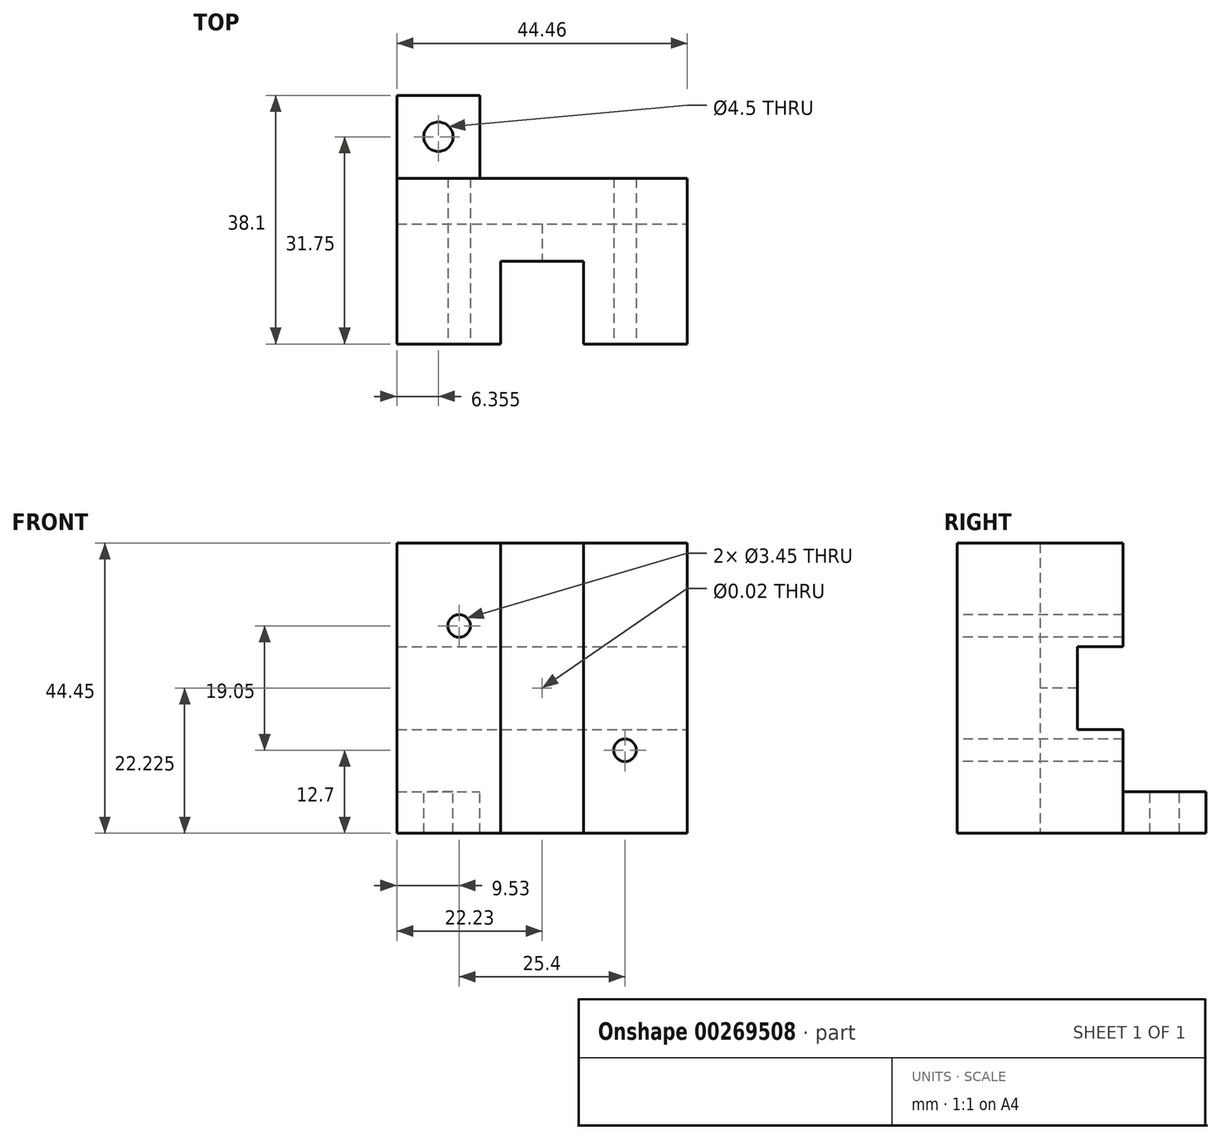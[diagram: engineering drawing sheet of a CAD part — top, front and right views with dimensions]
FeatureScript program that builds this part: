
annotation { "Feature Type Name" : "Feature", "Feature Type Description" : "" }
export const myFeature = defineFeature(function(context is Context, id is Id, definition is map)
    precondition{}
    {
        {
            var Q0;
            Q0=qCreatedBy(makeId("Top.planeOp"),FACE);
            var sketch = newSketch(context, id + "F0", { "sketchPlane" : qUnion([Q0])});
            skLineSegment(sketch, "E0.bottom", {"start": v(22.23, -12.7) * mm, "end": v(-22.23, -12.7) * mm});
            skLineSegment(sketch, "E0.top", {"start": v(22.23, 12.7) * mm, "end": v(-22.23, 12.7) * mm});
            skLineSegment(sketch, "E0.left", {"start": v(22.23, -12.7) * mm, "end": v(22.23, 12.7) * mm});
            skLineSegment(sketch, "E0.right", {"start": v(-22.23, -12.7) * mm, "end": v(-22.23, 12.7) * mm});
            skPoint(sketch, "E0.middle", {"position": v(0, 0) * mm});
            skSolve(sketch);
        }
        {
            var Q0;
            Q0=qSketchRegion(id+"F0",true);
            extrude(context, id + "F1", {"entities" : qUnion([Q0]), "depth" : 44.45 * mm});
        }
        {
            var Q0;
            Q0=makeQuery(id+"F1.opExtrude","SWEPT_FACE",FACE,{"disambiguationData":[OSD([sQuery(id+"F0.wireOp",EDGE,"E0.bottom")])]});
            var sketch = newSketch(context, id + "F2", { "sketchPlane" : qUnion([Q0])});
            skLineSegment(sketch, "E1.bottom", {"start": v(6.35, 44.45) * mm, "end": v(-6.35, 44.45) * mm});
            skLineSegment(sketch, "E1.top", {"start": v(6.35, 0) * mm, "end": v(-6.35, 0) * mm});
            skLineSegment(sketch, "E1.left", {"start": v(6.35, 44.45) * mm, "end": v(6.35, 0) * mm});
            skLineSegment(sketch, "E1.right", {"start": v(-6.35, 44.45) * mm, "end": v(-6.35, 0) * mm});
            skPoint(sketch, "E1.middle", {"position": v(0, 22.23) * mm});
            skSolve(sketch);
        }
        {
            var Q0;
            Q0=qSketchRegion(id+"F2",true);
            extrude(context, id + "F3", {"entities" : qUnion([Q0]), "operationType" : NewBodyOperationType.REMOVE, "oppositeDirection" : true, "depth" : 12.7 * mm});
        }
        {
            var Q0;
            Q0=makeQuery(id+"F1.opExtrude","SWEPT_FACE",FACE,{"disambiguationData":[OSD([sQuery(id+"F0.wireOp",EDGE,"E0.top")])]});
            var sketch = newSketch(context, id + "F4", { "sketchPlane" : qUnion([Q0])});
            skLineSegment(sketch, "E2.bottom", {"start": v(22.23, 15.88) * mm, "end": v(-22.23, 15.88) * mm});
            skLineSegment(sketch, "E2.top", {"start": v(22.23, 28.58) * mm, "end": v(-22.23, 28.58) * mm});
            skLineSegment(sketch, "E2.left", {"start": v(22.23, 15.88) * mm, "end": v(22.23, 28.58) * mm});
            skLineSegment(sketch, "E2.right", {"start": v(-22.23, 15.88) * mm, "end": v(-22.23, 28.58) * mm});
            skPoint(sketch, "E2.middle", {"position": v(0, 22.23) * mm});
            skPoint(sketch, "E2.middle.positionSnap0", {"position": v(22.23, 22.23) * mm});
            skPoint(sketch, "E2.middle.positionSnap1", {"position": v(0, 0) * mm});
            skPoint(sketch, "E2.centerSnap0", {"position": v(22.23, 22.23) * mm});
            skPoint(sketch, "E2.centerSnap1", {"position": v(0, 0) * mm});
            skSolve(sketch);
        }
        {
            var Q0;
            Q0=qSketchRegion(id+"F4",true);
            extrude(context, id + "F5", {"entities" : qUnion([Q0]), "operationType" : NewBodyOperationType.REMOVE, "oppositeDirection" : true, "depth" : 7 * mm});
        }
        {
            var Q0;
            {var subQ0=sQuery(id+"F0.wireOp",EDGE,"E0.right");var subQ3=sQuery(id+"F0.wireOp",EDGE,"E0.bottom");Q0=makeQuery(id+"F3.boolean.opBoolean","SPLIT",FACE,{"disambiguationData":[TD([makeQuery(id+"F1.opExtrude","SWEPT_FACE",FACE,{"disambiguationData":[OSD([subQ0])]})])],"derivedFrom":makeQuery(id+"F1.opExtrude","SWEPT_FACE",FACE,{"disambiguationData":[OSD([subQ3])]})});}
            var sketch = newSketch(context, id + "F6", { "sketchPlane" : qUnion([Q0])});
            skPoint(sketch, "E3", {"position": v(0, 22.23) * mm});
            skPoint(sketch, "E3.positionSnap0", {"position": v(-22.23, 22.23) * mm});
            skSolve(sketch);
        }
        {
            var Q0;
            Q0=sQuery(id+"F6.wireOp",VERTEX,"E3");
            var Q1;
            Q1=makeQuery(id+"F1.opExtrude","SWEPT_BODY",BODY,{"disambiguationData":[OSD([sQuery(id+"F0.wireOp",EDGE,"E0.bottom"),sQuery(id+"F0.wireOp",EDGE,"E0.top"),sQuery(id+"F0.wireOp",EDGE,"E0.left"),sQuery(id+"F0.wireOp",EDGE,"E0.right")])]});
            hole(context, id + "F7", {"style" : HoleStyle.SIMPLE, "endStyle" : HoleEndStyle.THROUGH, "standardTappedOrClearance" : lookupTablePath({ "standard" : "ANSI", "size" : "1/2 (0.5)", "type" : "Drilled" }), "standardBlindInLast" : lookupTablePath({ "standard" : "ANSI", "size" : "1/2", "type" : "Drilled" }), "holeDiameter" : 1 / 50.8 * mm, "tappedDepth" : 10.16 * mm, "tapClearance" : 3, "locations" : qUnion([Q0]), "scope" : qUnion([Q1])});
        }
        {
            var Q0;
            {var subQ2=sQuery(id+"F0.wireOp",EDGE,"E0.top");Q0=makeQuery(id+"F5.boolean.opBoolean","SPLIT",FACE,{"disambiguationData":[TD([makeQuery(id+"F5.opExtrude","SWEPT_FACE",FACE,{"disambiguationData":[OSD([sQuery(id+"F4.wireOp",EDGE,"E2.bottom")])]})])],"derivedFrom":makeQuery(id+"F1.opExtrude","SWEPT_FACE",FACE,{"disambiguationData":[OSD([subQ2])]})});}
            var sketch = newSketch(context, id + "F8", { "sketchPlane" : qUnion([Q0])});
            skLineSegment(sketch, "E4.bottom", {"start": v(22.23, 0) * mm, "end": v(9.52, 0) * mm});
            skLineSegment(sketch, "E4.top", {"start": v(22.23, 6.35) * mm, "end": v(9.52, 6.35) * mm});
            skLineSegment(sketch, "E4.left", {"start": v(22.23, 0) * mm, "end": v(22.23, 6.35) * mm});
            skLineSegment(sketch, "E4.right", {"start": v(9.53, 0) * mm, "end": v(9.52, 6.35) * mm});
            skSolve(sketch);
        }
        {
            var Q0;
            Q0=qSketchRegion(id+"F8",true);
            extrude(context, id + "F9", {"entities" : qUnion([Q0]), "operationType" : NewBodyOperationType.ADD, "depth" : 12.7 * mm});
        }
        {
            var Q0;
            Q0=makeQuery(id+"F9.opExtrude","SWEPT_FACE",FACE,{"disambiguationData":[OSD([sQuery(id+"F8.wireOp",EDGE,"E4.top")])]});
            var sketch = newSketch(context, id + "F10", { "sketchPlane" : qUnion([Q0])});
            skPoint(sketch, "E5", {"position": v(-15.88, 19.05) * mm});
            skPoint(sketch, "E5.positionSnap0", {"position": v(-15.88, 25.4) * mm});
            skPoint(sketch, "E5.positionSnap1", {"position": v(-9.53, 19.05) * mm});
            skSolve(sketch);
        }
        {
            var Q0;
            Q0=sQuery(id+"F10.wireOp",VERTEX,"E5");
            var Q1;
            Q1=makeQuery(id+"F1.opExtrude","SWEPT_BODY",BODY,{"disambiguationData":[OSD([sQuery(id+"F0.wireOp",EDGE,"E0.bottom"),sQuery(id+"F0.wireOp",EDGE,"E0.top"),sQuery(id+"F0.wireOp",EDGE,"E0.left"),sQuery(id+"F0.wireOp",EDGE,"E0.right")])]});
            hole(context, id + "F11", {"style" : HoleStyle.SIMPLE, "endStyle" : HoleEndStyle.THROUGH, "standardTappedOrClearance" : lookupTablePath({ "standard" : "ANSI", "fit" : "Normal (ASME)", "size" : "#8", "type" : "Clearance" }), "standardBlindInLast" : lookupTablePath({ "fit" : "Free", "standard" : "ANSI", "size" : "#8", "type" : "Clearance" }), "holeDiameter" : 4.5 * mm, "tappedDepth" : 9.52 * mm, "tapClearance" : 3, "locations" : qUnion([Q0]), "scope" : qUnion([Q1])});
        }
        {
            var Q0;
            {var subQ0=sQuery(id+"F0.wireOp",EDGE,"E0.right");var subQ3=sQuery(id+"F0.wireOp",EDGE,"E0.bottom");Q0=makeQuery(id+"F3.boolean.opBoolean","SPLIT",FACE,{"disambiguationData":[TD([makeQuery(id+"F1.opExtrude","SWEPT_FACE",FACE,{"disambiguationData":[OSD([subQ0])]})])],"derivedFrom":makeQuery(id+"F1.opExtrude","SWEPT_FACE",FACE,{"disambiguationData":[OSD([subQ3])]})});}
            var sketch = newSketch(context, id + "F12", { "sketchPlane" : qUnion([Q0])});
            skArc(sketch, "E6.0", {"start": v(-6.35, 22.23) * mm, "mid": v(0, 28.58) * mm, "end": v(6.35, 22.23) * mm, "construction": true});
            skArc(sketch, "E6.1", {"start": v(6.35, 22.23) * mm, "mid": v(0, 15.88) * mm, "end": v(-6.35, 22.23) * mm, "construction": true});
            skLineSegment(sketch, "E7.bottom", {"start": v(12.7, 31.75) * mm, "end": v(-12.7, 31.75) * mm, "construction": true});
            skLineSegment(sketch, "E7.top", {"start": v(12.7, 12.7) * mm, "end": v(-12.7, 12.7) * mm, "construction": true});
            skLineSegment(sketch, "E7.left", {"start": v(12.7, 31.75) * mm, "end": v(12.7, 12.7) * mm, "construction": true});
            skLineSegment(sketch, "E7.right", {"start": v(-12.7, 31.75) * mm, "end": v(-12.7, 12.7) * mm, "construction": true});
            skSolve(sketch);
        }
        {
            var Q0;
            Q0=sQuery(id+"F12.wireOp",VERTEX,"E7.right.start");
            var Q1;
            Q1=sQuery(id+"F12.wireOp",VERTEX,"E7.left.end");
            var Q2;
            Q2=makeQuery(id+"F1.opExtrude","SWEPT_BODY",BODY,{"disambiguationData":[OSD([sQuery(id+"F0.wireOp",EDGE,"E0.bottom"),sQuery(id+"F0.wireOp",EDGE,"E0.top"),sQuery(id+"F0.wireOp",EDGE,"E0.left"),sQuery(id+"F0.wireOp",EDGE,"E0.right")])]});
            hole(context, id + "F13", {"style" : HoleStyle.SIMPLE, "endStyle" : HoleEndStyle.THROUGH, "standardTappedOrClearance" : lookupTablePath({ "standard" : "ANSI", "engagement" : "75%", "pitch" : "32 tpi", "size" : "#8", "type" : "Tapped" }), "standardBlindInLast" : lookupTablePath({ "standard" : "ANSI", "engagement" : "75%", "pitch" : "32 tpi", "size" : "#8", "type" : "Tapped" }), "holeDiameter" : 3.45 * mm, "showTappedDepth" : true, "tappedDepth" : 10.16 * mm, "tapClearance" : 3, "locations" : qUnion([Q0, Q1]), "scope" : qUnion([Q2]), "majorDiameter" : 4.17 * mm});
        }
    });
